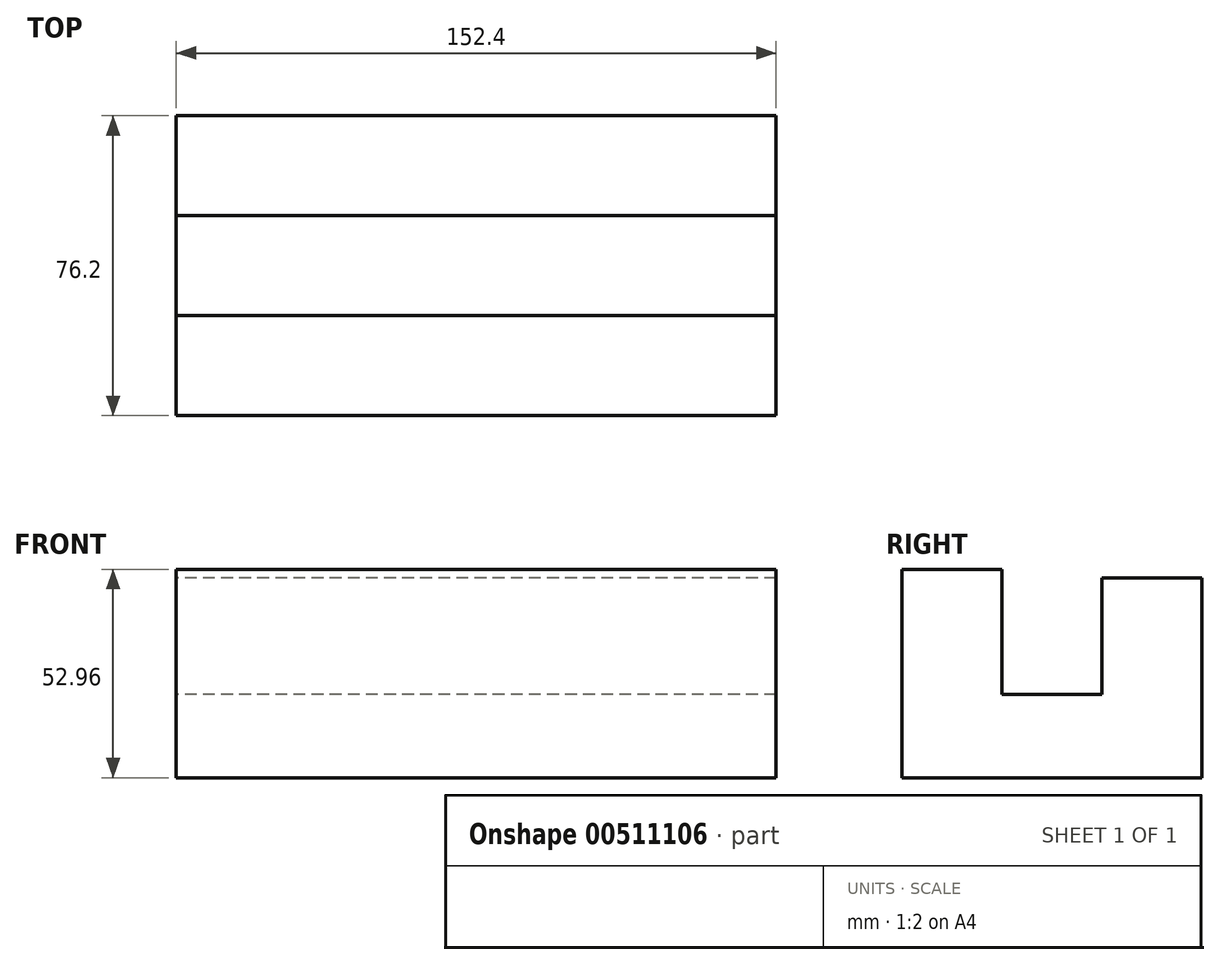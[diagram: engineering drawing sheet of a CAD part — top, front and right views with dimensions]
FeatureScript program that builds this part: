
annotation { "Feature Type Name" : "Feature", "Feature Type Description" : "" }
export const myFeature = defineFeature(function(context is Context, id is Id, definition is map)
    precondition{}
    {
        {
            var Q0;
            Q0=qCreatedBy(makeId("Right.planeOp"),FACE);
            var sketch = newSketch(context, id + "F0", { "sketchPlane" : qUnion([Q0])});
            skLineSegment(sketch, "E0", {"start": v(-76.99, 11.78) * mm, "end": v(-76.99, 64.74) * mm});
            skLineSegment(sketch, "E1", {"start": v(-76.99, 64.74) * mm, "end": v(-51.59, 64.74) * mm});
            skLineSegment(sketch, "E2", {"start": v(-51.59, 64.74) * mm, "end": v(-51.59, 32.88) * mm});
            skLineSegment(sketch, "E3", {"start": v(-51.59, 32.88) * mm, "end": v(-26.19, 32.88) * mm});
            skLineSegment(sketch, "E4", {"start": v(-26.19, 32.88) * mm, "end": v(-26.19, 62.58) * mm});
            skLineSegment(sketch, "E5", {"start": v(-26.19, 62.58) * mm, "end": v(-0.79, 62.58) * mm});
            skLineSegment(sketch, "E6", {"start": v(-0.79, 62.58) * mm, "end": v(-0.79, 11.78) * mm});
            skLineSegment(sketch, "E7", {"start": v(-0.79, 11.78) * mm, "end": v(-76.99, 11.78) * mm});
            skSolve(sketch);
        }
        {
            var Q0;
            Q0=makeQuery(id+"F0.imprint","IMPRINT",FACE,{"disambiguationData":[TD([[makeQuery(id+"F0.imprint","IMPRINT",EDGE,{"derivedFrom":sQuery(id+"F0.wireOp",EDGE,"E0")}),-1.0]])]});
            extrude(context, id + "F1", {"entities" : qUnion([Q0]), "depth" : 152.4 * mm});
        }
    });
